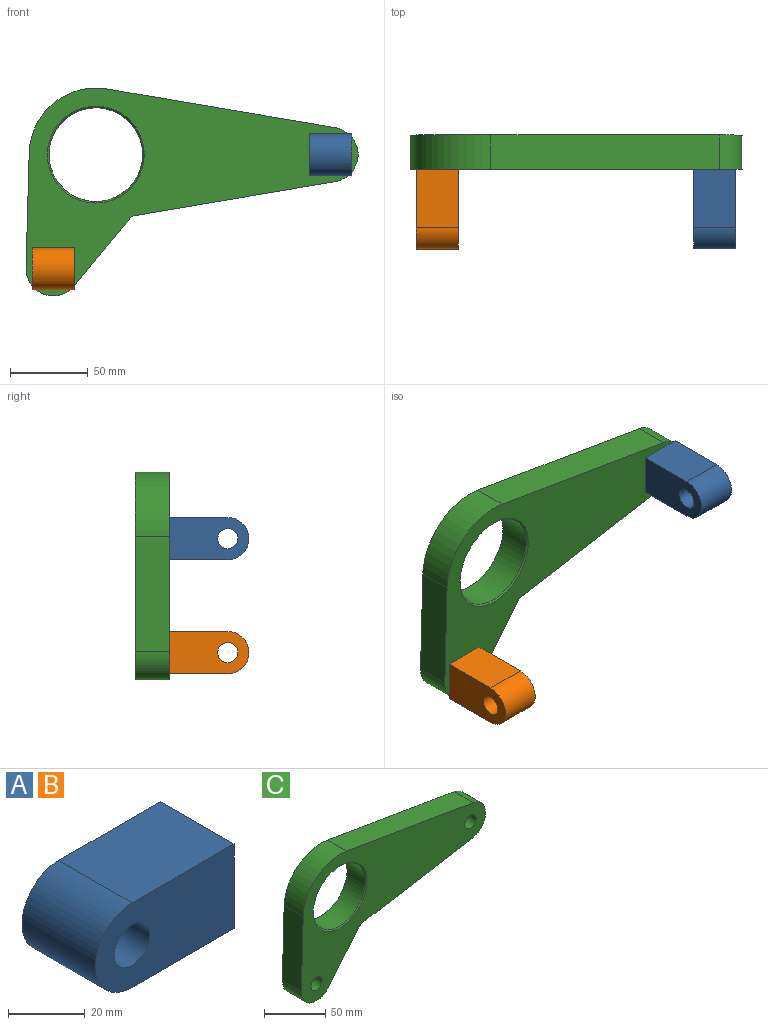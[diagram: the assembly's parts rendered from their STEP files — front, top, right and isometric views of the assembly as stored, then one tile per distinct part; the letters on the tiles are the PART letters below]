
ASSEMBLY  parts=3 mates=5
PART A: 9 faces, bbox 51x27x27 mm
  f0: plane 37.53x27mm, normal (0,0,1), area 1013.2mm2, adj f1,f3,f5,f6
  f1: cylinder r=13.5mm len=27mm, axis (0,1,0), area 1145.1mm2, adj f0,f2,f5,f6
  f2: plane 37.53x27mm, normal (0,0,-1), area 1013.2mm2, adj f1,f3,f5,f6
  f3: plane 27x27mm, normal (1,0,0), area 645.7mm2, adj f0,f2,f5,f6,f7
  f4: cylinder r=6.5mm len=27mm, axis (0,1,0), area 1102.7mm2, adj f5,f6
  f5: plane 51.03x27mm, normal (0,-1,0), area 1166.7mm2, adj f0,f1,f2,f3,f4
  f6: plane 51.03x27mm, normal (0,1,0), area 1166.7mm2, adj f0,f1,f2,f3,f4
  f7: cylinder r=5.15mm len=25.25mm, axis (1,0,0), area 817mm2, adj f3,f8
  f8: cone r=0mm half-angle=59deg, axis (1,0,0), area 97.2mm2, adj f7
PART B: same geometry as A
PART C: 14 faces, bbox 213x22x133.4 mm
  f0: cylinder r=17.5mm len=31.04mm, axis (0,1,0), area 956mm2, adj f1,f10,f11,f12
  f1: plane 42.92x35.16mm, normal (0.77,0,-0.63), area 1220.5mm2, adj f0,f2,f11,f12
  f2: cylinder r=6.35mm len=22mm, axis (0,1,0), area 100.1mm2, adj f1,f3,f11,f12
  f3: plane 128.37x22mm, normal (0.17,0,-0.99), area 2864.7mm2, adj f2,f4,f11,f12
  f4: cylinder r=17.5mm len=34.51mm, axis (0,1,0), area 1080mm2, adj f3,f5,f11,f12
  f5: plane 146.48x24.88mm, normal (0.17,0,0.99), area 3268.8mm2, adj f4,f6,f11,f12
  f6: cylinder r=42.74mm len=49.88mm, axis (0,1,0), area 1608.9mm2, adj f5,f10,f11,f12
  f7: cylinder r=30.04mm len=60.07mm, axis (0,1,0), area 3963.1mm2, adj f12,f13
  f8: cylinder r=6.5mm len=22mm, axis (0,1,0), area 898.5mm2, adj f11,f12
  f9: cylinder r=6.5mm len=22mm, axis (0,1,0), area 898.5mm2, adj f11,f12
  f10: plane 73.82x22mm, normal (-1,0,0.03), area 1624.6mm2, adj f0,f6,f11,f12
  f11: plane 212.99x133.35mm, normal (0,-1,0), area 11796.3mm2, adj f0,f1,f2,f3,f4,f5,f6,f8
  f12: plane 212.99x133.35mm, normal (0,1,0), area 11988.1mm2, adj f0,f1,f2,f3,f4,f5,f6,f7
  f13: cone r=30.04mm half-angle=45deg, axis (0,-1,0), area 271.3mm2, adj f7,f11
PLACE A rot(axis=(0,0,1),90deg) t=(149.85,-110.88,-25.75)mm
PLACE B rot(axis=(0,0,1),90deg) t=(-28.14,-110.88,-98.87)mm
PLACE C t=(-0.86,-99.88,-25.75)mm
MATE planar B.f7 <-> A.f7  axis (0,1,0) through (-28.14,-110.88,-98.87)mm
MATE planar B.f7 <-> C.f11  axis (0,1,0) through (-28.14,-110.88,-98.87)mm
MATE parallel A.f3 <-> C.f11  axis (0,1,0) through (163.35,-110.88,-25.75)mm
MATE cylindrical C.f0 <-> B.f7  axis (0,1,0) through (-28.14,-110.88,-98.87)mm
MATE cylindrical A.f7 <-> C.f8  axis (0,1,0) through (149.85,-123.5,-25.75)mm
